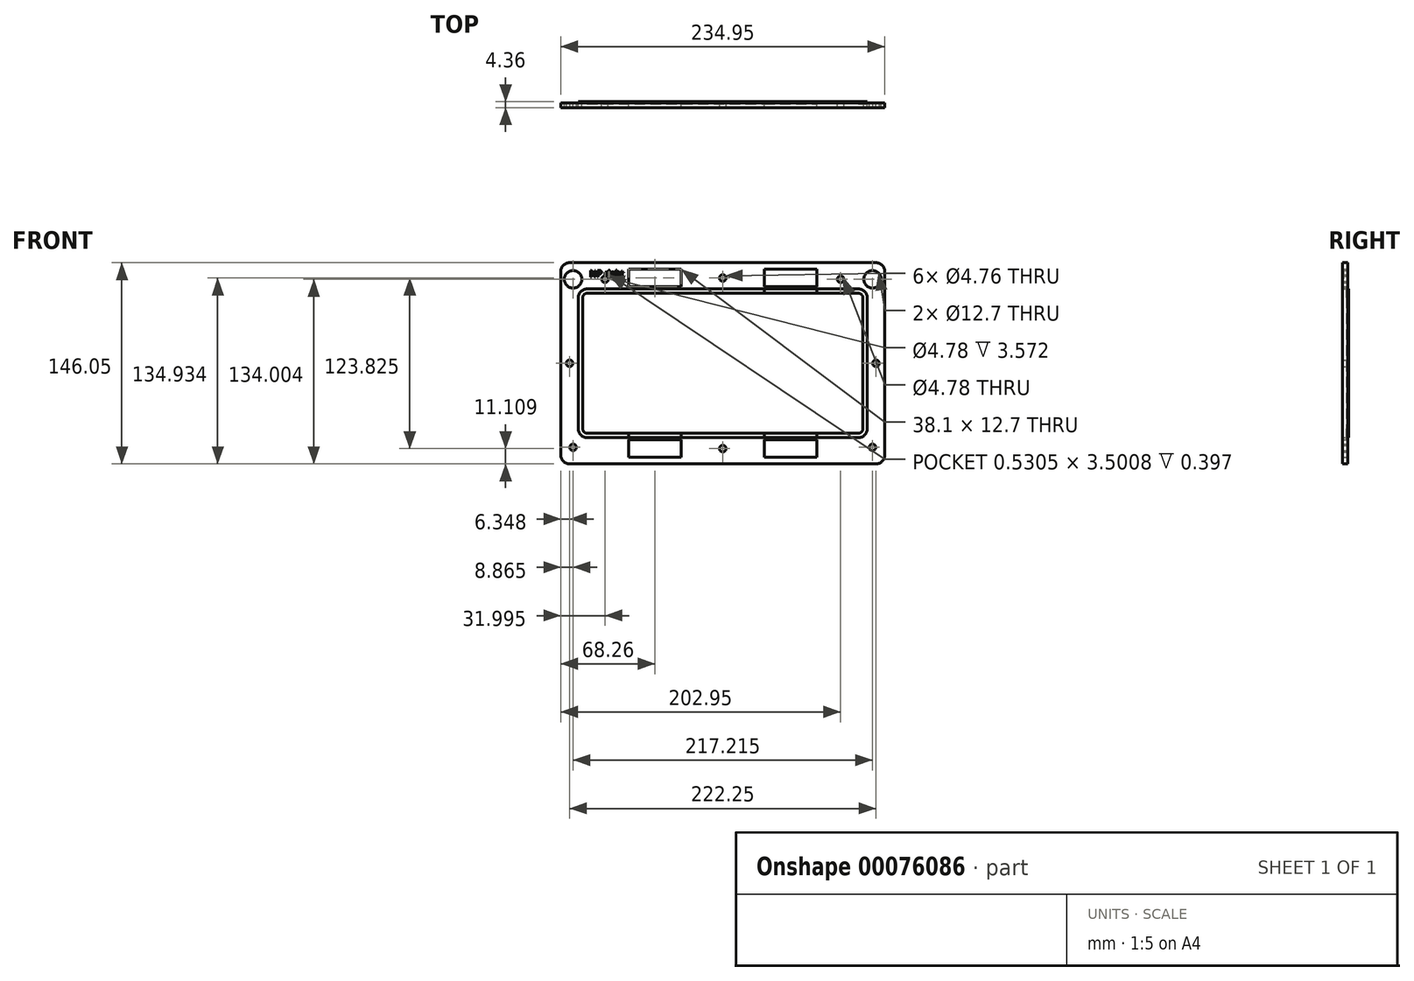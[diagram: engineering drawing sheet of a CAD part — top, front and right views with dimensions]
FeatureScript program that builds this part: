
annotation { "Feature Type Name" : "Feature", "Feature Type Description" : "" }
export const myFeature = defineFeature(function(context is Context, id is Id, definition is map)
    precondition{}
    {
        {
            var Q0;
            Q0=qCreatedBy(makeId("Front.planeOp"),FACE);
            var sketch = newSketch(context, id + "F0", { "sketchPlane" : qUnion([Q0])});
            skLineSegment(sketch, "E0.bottom", {"start": v(-150.65, 42.97) * mm, "end": v(46.2, 42.97) * mm});
            skLineSegment(sketch, "E0.top", {"start": v(-150.65, -64.98) * mm, "end": v(46.2, -64.98) * mm});
            skLineSegment(sketch, "E0.left", {"start": v(-157, 36.62) * mm, "end": v(-157, -58.63) * mm});
            skLineSegment(sketch, "E0.right", {"start": v(52.55, 36.62) * mm, "end": v(52.55, -58.63) * mm});
            skPoint(sketch, "E1.visualSharp", {"position": v(-157, 42.97) * mm});
            skArc(sketch, "E1.filletArc", {"start": v(-150.65, 42.97) * mm, "mid": v(-155.14, 41.1) * mm, "end": v(-157, 36.62) * mm});
            skPoint(sketch, "E2.visualSharp", {"position": v(52.55, 42.97) * mm});
            skArc(sketch, "E2.filletArc", {"start": v(52.55, 36.62) * mm, "mid": v(50.69, 41.1) * mm, "end": v(46.2, 42.97) * mm});
            skPoint(sketch, "E3.visualSharp", {"position": v(52.55, -64.98) * mm});
            skArc(sketch, "E3.filletArc", {"start": v(46.2, -64.98) * mm, "mid": v(50.69, -63.12) * mm, "end": v(52.55, -58.63) * mm});
            skPoint(sketch, "E4.visualSharp", {"position": v(-157, -64.98) * mm});
            skArc(sketch, "E4.filletArc", {"start": v(-157, -58.63) * mm, "mid": v(-155.14, -63.12) * mm, "end": v(-150.65, -64.98) * mm});
            skArc(sketch, "E5.0", {"start": v(-150.65, 39.8) * mm, "mid": v(-152.9, 38.86) * mm, "end": v(-153.83, 36.62) * mm});
            skLineSegment(sketch, "E5.1", {"start": v(-153.83, 36.62) * mm, "end": v(-153.83, -58.63) * mm});
            skLineSegment(sketch, "E5.2", {"start": v(-150.65, 39.8) * mm, "end": v(46.2, 39.8) * mm});
            skArc(sketch, "E5.3", {"start": v(-153.83, -58.63) * mm, "mid": v(-152.9, -60.88) * mm, "end": v(-150.65, -61.8) * mm});
            skArc(sketch, "E5.4", {"start": v(49.37, 36.62) * mm, "mid": v(48.44, 38.86) * mm, "end": v(46.2, 39.8) * mm});
            skLineSegment(sketch, "E5.5", {"start": v(49.37, 36.62) * mm, "end": v(49.37, -58.63) * mm});
            skArc(sketch, "E5.6", {"start": v(46.2, -61.8) * mm, "mid": v(48.44, -60.88) * mm, "end": v(49.37, -58.63) * mm});
            skLineSegment(sketch, "E5.7", {"start": v(-150.65, -61.8) * mm, "end": v(46.2, -61.8) * mm});
            skLineSegment(sketch, "E6.0", {"start": v(-163.35, 62.02) * mm, "end": v(58.9, 62.02) * mm});
            skLineSegment(sketch, "E7.0", {"start": v(-163.35, -84.03) * mm, "end": v(58.9, -84.03) * mm});
            skLineSegment(sketch, "E8.0", {"start": v(-169.7, 55.67) * mm, "end": v(-169.7, -77.68) * mm});
            skLineSegment(sketch, "E9.0", {"start": v(65.25, 55.67) * mm, "end": v(65.25, -77.68) * mm});
            skPoint(sketch, "E10.visualSharp", {"position": v(-169.7, 62.02) * mm});
            skArc(sketch, "E10.filletArc", {"start": v(-163.35, 62.02) * mm, "mid": v(-167.84, 60.16) * mm, "end": v(-169.7, 55.67) * mm});
            skPoint(sketch, "E11.visualSharp", {"position": v(65.25, 62.02) * mm});
            skArc(sketch, "E11.filletArc", {"start": v(65.25, 55.67) * mm, "mid": v(63.39, 60.16) * mm, "end": v(58.9, 62.02) * mm});
            skPoint(sketch, "E12.visualSharp", {"position": v(65.25, -84.03) * mm});
            skArc(sketch, "E12.filletArc", {"start": v(58.9, -84.03) * mm, "mid": v(63.39, -82.17) * mm, "end": v(65.25, -77.68) * mm});
            skPoint(sketch, "E13.visualSharp", {"position": v(-169.7, -84.03) * mm});
            skArc(sketch, "E13.filletArc", {"start": v(-169.7, -77.68) * mm, "mid": v(-167.84, -82.17) * mm, "end": v(-163.35, -84.03) * mm});
            skLineSegment(sketch, "E14", {"start": v(-169.7, 55.67) * mm, "end": v(-163.35, 62.02) * mm, "construction": true});
            skLineSegment(sketch, "E15", {"start": v(-166.53, 58.84) * mm, "end": v(-155.14, 41.1) * mm, "construction": true});
            skLineSegment(sketch, "E16", {"start": v(-169.7, -11) * mm, "end": v(-157, -11) * mm, "construction": true});
            skLineSegment(sketch, "E17", {"start": v(-163.35, -84.03) * mm, "end": v(-169.7, -77.68) * mm, "construction": true});
            skLineSegment(sketch, "E18", {"start": v(-166.53, -80.86) * mm, "end": v(-155.14, -63.12) * mm, "construction": true});
            skLineSegment(sketch, "E19", {"start": v(-52.23, 83.3) * mm, "end": v(-52.23, -151.32) * mm, "construction": true});
            skPoint(sketch, "E19.startSnap0", {"position": v(-52.23, 62.02) * mm});
            skLineSegment(sketch, "E20", {"start": v(-215.05, -11) * mm, "end": v(140.23, -11) * mm, "construction": true});
            skLineSegment(sketch, "E21", {"start": v(-150.65, 42.97) * mm, "end": v(-150.65, 62.02) * mm, "construction": true});
            skCircle(sketch, "E22", {"center": v(-160.83, 49.97) * mm, "radius": 6.35 * mm});
            skCircle(sketch, "E23", {"center": v(-163.35, -11) * mm, "radius": 2.38 * mm});
            skCircle(sketch, "E24", {"center": v(-160.83, -72) * mm, "radius": 2.38 * mm});
            skLineSegment(sketch, "E25", {"start": v(-150.65, -64.98) * mm, "end": v(-150.65, -84.03) * mm, "construction": true});
            skLineSegment(sketch, "E26", {"start": v(-150.65, -84.03) * mm, "end": v(-150.65, -74.5) * mm, "construction": true});
            skLineSegment(sketch, "E27", {"start": v(-150.65, -74.5) * mm, "end": v(-25.3, -74.5) * mm, "construction": true});
            skLineSegment(sketch, "E28", {"start": v(-52.23, 42.97) * mm, "end": v(-52.23, 62.02) * mm, "construction": true});
            skLineSegment(sketch, "E29", {"start": v(-52.23, -84.03) * mm, "end": v(-52.23, -64.98) * mm, "construction": true});
            skCircle(sketch, "E30", {"center": v(-52.23, 50.9) * mm, "radius": 2.38 * mm});
            skLineSegment(sketch, "E31.bottom", {"start": v(-82.39, 44.55) * mm, "end": v(-120.49, 44.55) * mm});
            skLineSegment(sketch, "E31.top", {"start": v(-82.39, 57.25) * mm, "end": v(-120.49, 57.25) * mm});
            skLineSegment(sketch, "E31.left", {"start": v(-82.39, 44.55) * mm, "end": v(-82.39, 57.25) * mm});
            skLineSegment(sketch, "E31.right", {"start": v(-120.49, 44.55) * mm, "end": v(-120.49, 57.25) * mm});
            skPoint(sketch, "E31.middle", {"position": v(-101.44, 50.9) * mm});
            skLineSegment(sketch, "E32.MirrorCS", {"start": v(-22.06, 44.55) * mm, "end": v(-22.06, 57.25) * mm});
            skLineSegment(sketch, "E33.MirrorCS", {"start": v(-22.06, 57.25) * mm, "end": v(16.04, 57.25) * mm});
            skLineSegment(sketch, "E34.MirrorCS", {"start": v(16.04, 44.55) * mm, "end": v(16.04, 57.25) * mm});
            skLineSegment(sketch, "E35.MirrorCS", {"start": v(-22.06, 44.55) * mm, "end": v(16.04, 44.55) * mm});
            skCircle(sketch, "E36.MirrorC", {"center": v(56.38, 49.97) * mm, "radius": 6.35 * mm});
            skCircle(sketch, "E37.MirrorC", {"center": v(58.9, -11) * mm, "radius": 2.38 * mm});
            skCircle(sketch, "E38.MirrorC", {"center": v(56.38, -72) * mm, "radius": 2.38 * mm});
            skLineSegment(sketch, "E39.MirrorCS", {"start": v(-120.49, -66.57) * mm, "end": v(-120.49, -79.27) * mm});
            skLineSegment(sketch, "E40.MirrorCS", {"start": v(-82.39, -66.57) * mm, "end": v(-82.39, -79.27) * mm});
            skLineSegment(sketch, "E41.MirrorCS", {"start": v(-82.39, -66.57) * mm, "end": v(-120.49, -66.57) * mm});
            skLineSegment(sketch, "E42.MirrorCS", {"start": v(-82.39, -79.27) * mm, "end": v(-120.49, -79.27) * mm});
            skCircle(sketch, "E43.MirrorC", {"center": v(-52.23, -72.92) * mm, "radius": 2.38 * mm});
            skLineSegment(sketch, "E44.MirrorCS", {"start": v(-22.06, -66.57) * mm, "end": v(-22.06, -79.27) * mm});
            skLineSegment(sketch, "E45.MirrorCS", {"start": v(-22.06, -79.27) * mm, "end": v(16.04, -79.27) * mm});
            skLineSegment(sketch, "E46.MirrorCS", {"start": v(16.04, -66.57) * mm, "end": v(16.04, -79.27) * mm});
            skLineSegment(sketch, "E47.MirrorCS", {"start": v(-22.06, -66.57) * mm, "end": v(16.04, -66.57) * mm});
            skLineSegment(sketch, "E48", {"start": v(-160.83, 49.97) * mm, "end": v(56.38, 49.97) * mm, "construction": true});
            skCircle(sketch, "E49", {"center": v(-137.7, 49.97) * mm, "radius": 2.39 * mm});
            skCircle(sketch, "E50", {"center": v(33.25, 49.97) * mm, "radius": 2.39 * mm});
            skSolve(sketch);
        }
        {
            var Q0;
            Q0 = qSketchRegion(id + "F0", true);
            var Q1;
            Q1=makeQuery(id+"F0.imprint","IMPRINT",FACE,{"disambiguationData":[TD([[makeQuery(id+"F0.imprint","IMPRINT",EDGE,{"derivedFrom":sQuery(id+"F0.wireOp",EDGE,"E0.bottom")}),-1.0]])]});
            extrude(context, id + "F1", {"entities" : qUnion([Q0, Q1]), "depth" : 0.8 * mm});
        }
        {
            var Q0;
            Q0=makeQuery(id+"F0.imprint","IMPRINT",FACE,{"disambiguationData":[TD([[makeQuery(id+"F0.imprint","IMPRINT",EDGE,{"derivedFrom":sQuery(id+"F0.wireOp",EDGE,"E0.bottom")}),1.0]])]});
            var sketch = newSketch(context, id + "F2", { "sketchPlane" : qUnion([Q0])});
            skArc(sketch, "E51.0", {"start": v(-150.65, 42.97) * mm, "mid": v(-155.14, 41.1) * mm, "end": v(-157, 36.62) * mm});
            skLineSegment(sketch, "E51.1", {"start": v(-157, 36.62) * mm, "end": v(-157, -58.63) * mm});
            skLineSegment(sketch, "E51.2", {"start": v(-150.65, 42.97) * mm, "end": v(46.2, 42.97) * mm});
            skArc(sketch, "E51.3", {"start": v(-157, -58.63) * mm, "mid": v(-155.14, -63.12) * mm, "end": v(-150.65, -64.98) * mm});
            skArc(sketch, "E51.4", {"start": v(52.55, 36.62) * mm, "mid": v(50.69, 41.1) * mm, "end": v(46.2, 42.97) * mm});
            skLineSegment(sketch, "E51.5", {"start": v(52.55, 36.62) * mm, "end": v(52.55, -58.63) * mm});
            skArc(sketch, "E51.6", {"start": v(46.2, -64.98) * mm, "mid": v(50.69, -63.12) * mm, "end": v(52.55, -58.63) * mm});
            skLineSegment(sketch, "E51.7", {"start": v(-150.65, -64.98) * mm, "end": v(46.2, -64.98) * mm});
            skArc(sketch, "E52.0", {"start": v(49.37, 36.62) * mm, "mid": v(48.44, 38.86) * mm, "end": v(46.2, 39.8) * mm});
            skLineSegment(sketch, "E52.1", {"start": v(-150.65, 39.8) * mm, "end": v(46.2, 39.8) * mm});
            skLineSegment(sketch, "E52.2", {"start": v(49.37, 36.62) * mm, "end": v(49.37, -58.63) * mm});
            skArc(sketch, "E52.3", {"start": v(-150.65, 39.8) * mm, "mid": v(-152.9, 38.86) * mm, "end": v(-153.83, 36.62) * mm});
            skArc(sketch, "E52.4", {"start": v(46.2, -61.8) * mm, "mid": v(48.44, -60.88) * mm, "end": v(49.37, -58.63) * mm});
            skLineSegment(sketch, "E52.5", {"start": v(-150.65, -61.8) * mm, "end": v(46.2, -61.8) * mm});
            skArc(sketch, "E52.6", {"start": v(-153.83, -58.63) * mm, "mid": v(-152.9, -60.88) * mm, "end": v(-150.65, -61.8) * mm});
            skLineSegment(sketch, "E52.7", {"start": v(-153.83, 36.62) * mm, "end": v(-153.83, -58.63) * mm});
            skSolve(sketch);
        }
        {
            var Q0;
            Q0 = qSketchRegion(id + "F0", true);
            extrude(context, id + "F3", {"entities" : qUnion([Q0]), "operationType" : NewBodyOperationType.ADD, "depth" : 3.57 * mm});
        }
        {
            var Q0;
            Q0=makeQuery(id+"F1.opExtrude","CAP_FACE",FACE,{"disambiguationData":[OSD([sQuery(id+"F0.wireOp",EDGE,"E5.0"),sQuery(id+"F0.wireOp",EDGE,"E5.1"),sQuery(id+"F0.wireOp",EDGE,"E5.2"),sQuery(id+"F0.wireOp",EDGE,"E5.3"),sQuery(id+"F0.wireOp",EDGE,"E5.4"),sQuery(id+"F0.wireOp",EDGE,"E5.5"),sQuery(id+"F0.wireOp",EDGE,"E5.6"),sQuery(id+"F0.wireOp",EDGE,"E5.7"),sQuery(id+"F0.wireOp",EDGE,"E6.0"),sQuery(id+"F0.wireOp",EDGE,"E7.0"),sQuery(id+"F0.wireOp",EDGE,"E8.0"),sQuery(id+"F0.wireOp",EDGE,"E9.0"),sQuery(id+"F0.wireOp",EDGE,"E10.filletArc"),sQuery(id+"F0.wireOp",EDGE,"E11.filletArc"),sQuery(id+"F0.wireOp",EDGE,"E12.filletArc"),sQuery(id+"F0.wireOp",EDGE,"E13.filletArc"),sQuery(id+"F0.wireOp",EDGE,"E22"),sQuery(id+"F0.wireOp",EDGE,"E23"),sQuery(id+"F0.wireOp",EDGE,"E24"),sQuery(id+"F0.wireOp",EDGE,"E30"),sQuery(id+"F0.wireOp",EDGE,"E31.bottom"),sQuery(id+"F0.wireOp",EDGE,"E31.top"),sQuery(id+"F0.wireOp",EDGE,"E31.left"),sQuery(id+"F0.wireOp",EDGE,"E31.right"),sQuery(id+"F0.wireOp",EDGE,"E32.MirrorCS"),sQuery(id+"F0.wireOp",EDGE,"E33.MirrorCS"),sQuery(id+"F0.wireOp",EDGE,"E34.MirrorCS"),sQuery(id+"F0.wireOp",EDGE,"E35.MirrorCS"),sQuery(id+"F0.wireOp",EDGE,"E36.MirrorC"),sQuery(id+"F0.wireOp",EDGE,"E37.MirrorC"),sQuery(id+"F0.wireOp",EDGE,"E38.MirrorC"),sQuery(id+"F0.wireOp",EDGE,"E39.MirrorCS"),sQuery(id+"F0.wireOp",EDGE,"E40.MirrorCS"),sQuery(id+"F0.wireOp",EDGE,"E41.MirrorCS"),sQuery(id+"F0.wireOp",EDGE,"E42.MirrorCS"),sQuery(id+"F0.wireOp",EDGE,"E43.MirrorC"),sQuery(id+"F0.wireOp",EDGE,"E44.MirrorCS"),sQuery(id+"F0.wireOp",EDGE,"E45.MirrorCS"),sQuery(id+"F0.wireOp",EDGE,"E46.MirrorCS"),sQuery(id+"F0.wireOp",EDGE,"E47.MirrorCS")])],"isStart":true});
            var sketch = newSketch(context, id + "F4", { "sketchPlane" : qUnion([Q0])});
            skLineSegment(sketch, "E53.bottom", {"start": v(-16.04, 44.55) * mm, "end": v(22.06, 44.55) * mm});
            skLineSegment(sketch, "E53.top", {"start": v(-16.04, 38.1) * mm, "end": v(22.06, 38.1) * mm});
            skLineSegment(sketch, "E53.left", {"start": v(-16.04, 44.55) * mm, "end": v(-16.04, 38.1) * mm});
            skLineSegment(sketch, "E53.right", {"start": v(22.06, 44.55) * mm, "end": v(22.06, 38.1) * mm});
            skLineSegment(sketch, "E54.bottom", {"start": v(-16.04, -66.57) * mm, "end": v(22.06, -66.57) * mm});
            skLineSegment(sketch, "E54.top", {"start": v(-16.04, -59.3) * mm, "end": v(22.06, -59.3) * mm});
            skLineSegment(sketch, "E54.left", {"start": v(-16.04, -66.57) * mm, "end": v(-16.04, -59.3) * mm});
            skLineSegment(sketch, "E54.right", {"start": v(22.06, -66.57) * mm, "end": v(22.06, -59.3) * mm});
            skLineSegment(sketch, "E55.bottom", {"start": v(82.39, -66.57) * mm, "end": v(120.49, -66.57) * mm});
            skLineSegment(sketch, "E55.top", {"start": v(82.39, -59.3) * mm, "end": v(120.49, -59.3) * mm});
            skLineSegment(sketch, "E55.left", {"start": v(82.39, -66.57) * mm, "end": v(82.39, -59.3) * mm});
            skLineSegment(sketch, "E55.right", {"start": v(120.49, -66.57) * mm, "end": v(120.49, -59.3) * mm});
            skSolve(sketch);
        }
        {
            var Q0;
            Q0 = qSketchRegion(id + "F4", true);
            extrude(context, id + "F5", {"entities" : qUnion([Q0]), "operationType" : NewBodyOperationType.REMOVE, "oppositeDirection" : true, "depth" : 0.8 * mm});
        }
        {
            var Q0;
            Q0 = qSketchRegion(id + "F2", true);
            extrude(context, id + "F6", {"entities" : qUnion([Q0]), "operationType" : NewBodyOperationType.ADD, "oppositeDirection" : true, "depth" : 0.8 * mm});
        }
        {
            var Q0;
            Q0=makeQuery(id+"F3.opExtrude","CAP_FACE",FACE,{"disambiguationData":[OSD([sQuery(id+"F0.wireOp",EDGE,"E0.bottom"),sQuery(id+"F0.wireOp",EDGE,"E0.top"),sQuery(id+"F0.wireOp",EDGE,"E0.left"),sQuery(id+"F0.wireOp",EDGE,"E0.right"),sQuery(id+"F0.wireOp",EDGE,"E1.filletArc"),sQuery(id+"F0.wireOp",EDGE,"E2.filletArc"),sQuery(id+"F0.wireOp",EDGE,"E3.filletArc"),sQuery(id+"F0.wireOp",EDGE,"E4.filletArc"),sQuery(id+"F0.wireOp",EDGE,"E6.0"),sQuery(id+"F0.wireOp",EDGE,"E7.0"),sQuery(id+"F0.wireOp",EDGE,"E8.0"),sQuery(id+"F0.wireOp",EDGE,"E9.0"),sQuery(id+"F0.wireOp",EDGE,"E10.filletArc"),sQuery(id+"F0.wireOp",EDGE,"E11.filletArc"),sQuery(id+"F0.wireOp",EDGE,"E12.filletArc"),sQuery(id+"F0.wireOp",EDGE,"E13.filletArc"),sQuery(id+"F0.wireOp",EDGE,"E22"),sQuery(id+"F0.wireOp",EDGE,"E23"),sQuery(id+"F0.wireOp",EDGE,"E24"),sQuery(id+"F0.wireOp",EDGE,"E30"),sQuery(id+"F0.wireOp",EDGE,"E31.bottom"),sQuery(id+"F0.wireOp",EDGE,"E31.top"),sQuery(id+"F0.wireOp",EDGE,"E31.left"),sQuery(id+"F0.wireOp",EDGE,"E31.right"),sQuery(id+"F0.wireOp",EDGE,"E32.MirrorCS"),sQuery(id+"F0.wireOp",EDGE,"E33.MirrorCS"),sQuery(id+"F0.wireOp",EDGE,"E34.MirrorCS"),sQuery(id+"F0.wireOp",EDGE,"E35.MirrorCS"),sQuery(id+"F0.wireOp",EDGE,"E36.MirrorC"),sQuery(id+"F0.wireOp",EDGE,"E37.MirrorC"),sQuery(id+"F0.wireOp",EDGE,"E38.MirrorC"),sQuery(id+"F0.wireOp",EDGE,"E39.MirrorCS"),sQuery(id+"F0.wireOp",EDGE,"E40.MirrorCS"),sQuery(id+"F0.wireOp",EDGE,"E41.MirrorCS"),sQuery(id+"F0.wireOp",EDGE,"E42.MirrorCS"),sQuery(id+"F0.wireOp",EDGE,"E43.MirrorC"),sQuery(id+"F0.wireOp",EDGE,"E44.MirrorCS"),sQuery(id+"F0.wireOp",EDGE,"E45.MirrorCS"),sQuery(id+"F0.wireOp",EDGE,"E46.MirrorCS"),sQuery(id+"F0.wireOp",EDGE,"E47.MirrorCS")])],"isStart":false});
            var sketch = newSketch(context, id + "F7", { "sketchPlane" : qUnion([Q0])});
            skText(sketch, "E56", { "text": "NP right\n", "fontName": "OpenSans-Regular.ttf"});
            const initialGuessF7  = {"E56": [-0.1488, 0.05177, 1, 0, 0.00471]};
            skSetInitialGuess(sketch, initialGuessF7);
            skSolve(sketch);
        }
        {
            var Q0;
            Q0 = qSketchRegion(id + "F7", true);
            extrude(context, id + "F8", {"entities" : qUnion([Q0]), "operationType" : NewBodyOperationType.REMOVE, "oppositeDirection" : true, "depth" : 0.4 * mm});
        }
    });
